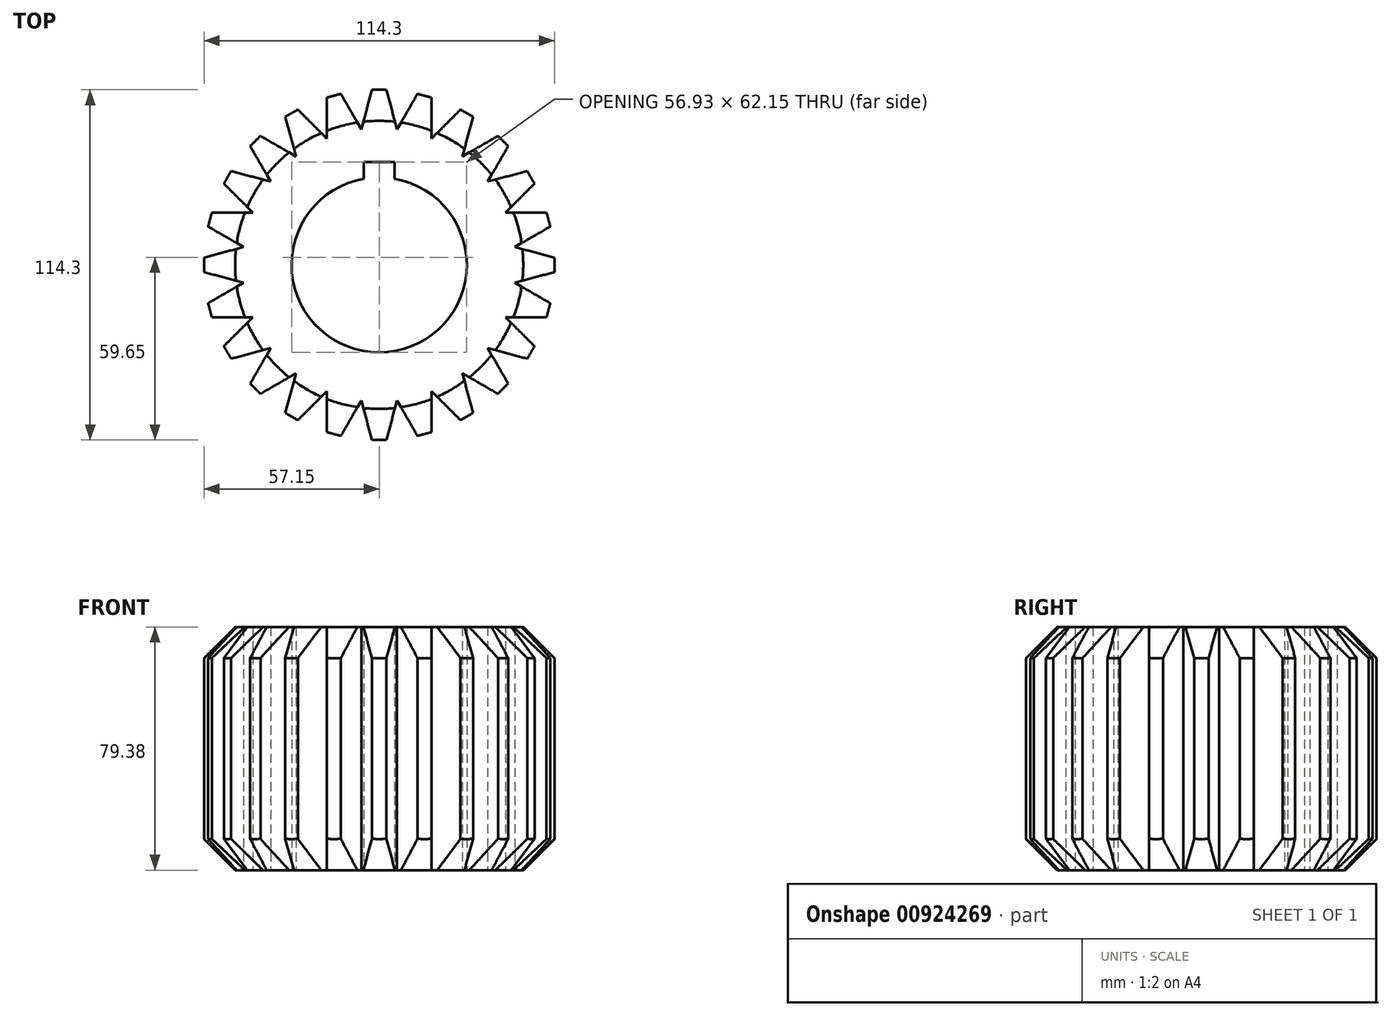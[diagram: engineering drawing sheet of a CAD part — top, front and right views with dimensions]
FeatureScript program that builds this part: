
annotation { "Feature Type Name" : "Feature", "Feature Type Description" : "" }
export const myFeature = defineFeature(function(context is Context, id is Id, definition is map)
    precondition{}
    {
        {
            var Q0;
            Q0=qCreatedBy(makeId("Top.planeOp"),FACE);
            var sketch = newSketch(context, id + "F0", { "sketchPlane" : qUnion([Q0])});
            skLineSegment(sketch, "E0", {"start": v(0, 57.15) * mm, "end": v(0, -57.15) * mm, "construction": true});
            skLineSegment(sketch, "E1", {"start": v(0, 0) * mm, "end": v(-7.32, 55.6) * mm, "construction": true});
            skLineSegment(sketch, "E2", {"start": v(-2.36, 57.15) * mm, "end": v(2.36, 57.15) * mm});
            skLineSegment(sketch, "E3", {"start": v(-2.36, 57.15) * mm, "end": v(-5.82, 44.23) * mm});
            skLineSegment(sketch, "E4.MirrorCS", {"start": v(-12.5, 55.81) * mm, "end": v(-5.82, 44.23) * mm});
            skLineSegment(sketch, "E5.MirrorCS", {"start": v(-12.5, 55.81) * mm, "end": v(-17.07, 54.6) * mm});
            skLineSegment(sketch, "E6.MirrorCS", {"start": v(-14.8, 55.2) * mm, "end": v(14.8, -55.2) * mm, "construction": true});
            skLineSegment(sketch, "E7.MirrorCS", {"start": v(2.36, 57.15) * mm, "end": v(5.82, 44.23) * mm});
            skLineSegment(sketch, "E8.MirrorCS", {"start": v(12.5, 55.81) * mm, "end": v(5.82, 44.23) * mm});
            skLineSegment(sketch, "E9.MirrorCS", {"start": v(12.5, 55.81) * mm, "end": v(17.07, 54.6) * mm});
            skLineSegment(sketch, "E10.MirrorCS", {"start": v(-17.07, 54.6) * mm, "end": v(-17.07, 41.22) * mm});
            skLineSegment(sketch, "E11.MirrorCS", {"start": v(17.07, 54.6) * mm, "end": v(17.07, 41.22) * mm});
            skLineSegment(sketch, "E12.MirrorCS", {"start": v(-28.58, 49.5) * mm, "end": v(28.58, -49.5) * mm, "construction": true});
            skLineSegment(sketch, "E13.MirrorCS", {"start": v(-38.74, 42.08) * mm, "end": v(-27.16, 35.4) * mm});
            skLineSegment(sketch, "E14.MirrorCS", {"start": v(-42.08, 38.74) * mm, "end": v(-35.4, 27.16) * mm});
            skLineSegment(sketch, "E15.MirrorCS", {"start": v(-42.08, 38.74) * mm, "end": v(-38.74, 42.08) * mm});
            skLineSegment(sketch, "E16.MirrorCS", {"start": v(-48.31, 30.62) * mm, "end": v(-35.4, 27.16) * mm});
            skLineSegment(sketch, "E17.MirrorCS", {"start": v(-48.31, 30.62) * mm, "end": v(-50.67, 26.53) * mm});
            skLineSegment(sketch, "E18.MirrorCS", {"start": v(-50.67, 26.53) * mm, "end": v(-41.22, 17.07) * mm});
            skLineSegment(sketch, "E19.MirrorCS", {"start": v(-54.6, 17.07) * mm, "end": v(-41.22, 17.07) * mm});
            skLineSegment(sketch, "E20.MirrorCS", {"start": v(-54.6, 17.07) * mm, "end": v(-55.81, 12.5) * mm});
            skLineSegment(sketch, "E21.MirrorCS", {"start": v(-55.81, 12.5) * mm, "end": v(-44.23, 5.82) * mm});
            skLineSegment(sketch, "E22.MirrorCS", {"start": v(-26.53, 50.67) * mm, "end": v(-17.07, 41.22) * mm});
            skLineSegment(sketch, "E23.MirrorCS", {"start": v(-30.62, 48.31) * mm, "end": v(-27.16, 35.4) * mm});
            skLineSegment(sketch, "E24.MirrorCS", {"start": v(-26.53, 50.67) * mm, "end": v(-30.62, 48.31) * mm});
            skLineSegment(sketch, "E25.MirrorCS", {"start": v(26.53, 50.67) * mm, "end": v(17.07, 41.22) * mm});
            skLineSegment(sketch, "E26.MirrorCS", {"start": v(26.53, 50.67) * mm, "end": v(30.62, 48.31) * mm});
            skLineSegment(sketch, "E27.MirrorCS", {"start": v(30.62, 48.31) * mm, "end": v(27.16, 35.4) * mm});
            skLineSegment(sketch, "E28.MirrorCS", {"start": v(38.74, 42.08) * mm, "end": v(27.16, 35.4) * mm});
            skLineSegment(sketch, "E29.MirrorCS", {"start": v(38.74, 42.08) * mm, "end": v(42.08, 38.74) * mm});
            skLineSegment(sketch, "E30.MirrorCS", {"start": v(42.08, 38.74) * mm, "end": v(35.4, 27.16) * mm});
            skLineSegment(sketch, "E31.MirrorCS", {"start": v(-57.15, 2.36) * mm, "end": v(-44.23, 5.82) * mm});
            skLineSegment(sketch, "E32.MirrorCS", {"start": v(-57.15, -2.36) * mm, "end": v(-44.23, -5.82) * mm});
            skLineSegment(sketch, "E33.MirrorCS", {"start": v(-57.15, 2.36) * mm, "end": v(-57.15, -2.36) * mm});
            skLineSegment(sketch, "E34", {"start": v(57.15, 0) * mm, "end": v(-57.15, 0) * mm, "construction": true});
            skLineSegment(sketch, "E35.MirrorCS", {"start": v(-55.81, -12.5) * mm, "end": v(-44.23, -5.82) * mm});
            skLineSegment(sketch, "E36.MirrorCS", {"start": v(-54.6, -17.07) * mm, "end": v(-55.81, -12.5) * mm});
            skLineSegment(sketch, "E37.MirrorCS", {"start": v(-50.67, -26.53) * mm, "end": v(-41.22, -17.07) * mm});
            skLineSegment(sketch, "E38.MirrorCS", {"start": v(-48.31, -30.62) * mm, "end": v(-50.67, -26.53) * mm});
            skLineSegment(sketch, "E39.MirrorCS", {"start": v(-48.31, -30.62) * mm, "end": v(-35.4, -27.16) * mm});
            skLineSegment(sketch, "E40.MirrorCS", {"start": v(-42.08, -38.74) * mm, "end": v(-35.4, -27.16) * mm});
            skLineSegment(sketch, "E41.MirrorCS", {"start": v(-42.08, -38.74) * mm, "end": v(-38.74, -42.08) * mm});
            skLineSegment(sketch, "E42.MirrorCS", {"start": v(-38.74, -42.08) * mm, "end": v(-27.16, -35.4) * mm});
            skLineSegment(sketch, "E43.MirrorCS", {"start": v(-30.62, -48.31) * mm, "end": v(-27.16, -35.4) * mm});
            skLineSegment(sketch, "E44.MirrorCS", {"start": v(-26.53, -50.67) * mm, "end": v(-30.62, -48.31) * mm});
            skLineSegment(sketch, "E45.MirrorCS", {"start": v(-26.53, -50.67) * mm, "end": v(-17.07, -41.22) * mm});
            skLineSegment(sketch, "E46.MirrorCS", {"start": v(-17.07, -54.6) * mm, "end": v(-17.07, -41.22) * mm});
            skLineSegment(sketch, "E47.MirrorCS", {"start": v(-14.8, -55.2) * mm, "end": v(14.8, 55.2) * mm, "construction": true});
            skLineSegment(sketch, "E48.MirrorCS", {"start": v(-12.5, -55.81) * mm, "end": v(-17.07, -54.6) * mm});
            skLineSegment(sketch, "E49.MirrorCS", {"start": v(-12.5, -55.81) * mm, "end": v(-5.82, -44.23) * mm});
            skLineSegment(sketch, "E50.MirrorCS", {"start": v(-2.36, -57.15) * mm, "end": v(-5.82, -44.23) * mm});
            skLineSegment(sketch, "E51.MirrorCS", {"start": v(-2.36, -57.15) * mm, "end": v(2.36, -57.15) * mm});
            skLineSegment(sketch, "E52.MirrorCS", {"start": v(-54.6, -17.07) * mm, "end": v(-41.22, -17.07) * mm});
            skLineSegment(sketch, "E53.MirrorCS", {"start": v(2.36, -57.15) * mm, "end": v(5.82, -44.23) * mm});
            skLineSegment(sketch, "E54.MirrorCS", {"start": v(12.5, -55.81) * mm, "end": v(17.07, -54.6) * mm});
            skLineSegment(sketch, "E55.MirrorCS", {"start": v(17.07, -54.6) * mm, "end": v(17.07, -41.22) * mm});
            skLineSegment(sketch, "E56.MirrorCS", {"start": v(26.53, -50.67) * mm, "end": v(17.07, -41.22) * mm});
            skLineSegment(sketch, "E57.MirrorCS", {"start": v(26.53, -50.67) * mm, "end": v(30.62, -48.31) * mm});
            skLineSegment(sketch, "E58.MirrorCS", {"start": v(30.62, -48.31) * mm, "end": v(27.16, -35.4) * mm});
            skLineSegment(sketch, "E59.MirrorCS", {"start": v(12.5, -55.81) * mm, "end": v(5.82, -44.23) * mm});
            skLineSegment(sketch, "E60.MirrorCS", {"start": v(38.74, -42.08) * mm, "end": v(27.16, -35.4) * mm});
            skLineSegment(sketch, "E61.MirrorCS", {"start": v(42.08, -38.74) * mm, "end": v(38.74, -42.08) * mm});
            skLineSegment(sketch, "E62.MirrorCS", {"start": v(42.08, -38.74) * mm, "end": v(35.4, -27.16) * mm});
            skLineSegment(sketch, "E63.MirrorCS", {"start": v(48.31, -30.62) * mm, "end": v(35.4, -27.16) * mm});
            skLineSegment(sketch, "E64.MirrorCS", {"start": v(48.31, -30.62) * mm, "end": v(50.67, -26.53) * mm});
            skLineSegment(sketch, "E65.MirrorCS", {"start": v(50.67, -26.53) * mm, "end": v(41.22, -17.07) * mm});
            skLineSegment(sketch, "E66.MirrorCS", {"start": v(54.6, -17.07) * mm, "end": v(41.22, -17.07) * mm});
            skLineSegment(sketch, "E67.MirrorCS", {"start": v(54.6, -17.07) * mm, "end": v(55.81, -12.5) * mm});
            skLineSegment(sketch, "E68.MirrorCS", {"start": v(55.81, -12.5) * mm, "end": v(44.23, -5.82) * mm});
            skLineSegment(sketch, "E69.MirrorCS", {"start": v(57.15, -2.36) * mm, "end": v(44.23, -5.82) * mm});
            skLineSegment(sketch, "E70.MirrorCS", {"start": v(57.15, 2.36) * mm, "end": v(57.15, -2.36) * mm});
            skLineSegment(sketch, "E71.MirrorCS", {"start": v(57.15, 2.36) * mm, "end": v(44.23, 5.82) * mm});
            skLineSegment(sketch, "E72.MirrorCS", {"start": v(55.81, 12.5) * mm, "end": v(44.23, 5.82) * mm});
            skLineSegment(sketch, "E73.MirrorCS", {"start": v(54.6, 17.07) * mm, "end": v(55.81, 12.5) * mm});
            skLineSegment(sketch, "E74.MirrorCS", {"start": v(48.31, 30.62) * mm, "end": v(35.4, 27.16) * mm});
            skLineSegment(sketch, "E75.MirrorCS", {"start": v(54.6, 17.07) * mm, "end": v(41.22, 17.07) * mm});
            skLineSegment(sketch, "E76.MirrorCS", {"start": v(50.67, 26.53) * mm, "end": v(41.22, 17.07) * mm});
            skLineSegment(sketch, "E77.MirrorCS", {"start": v(48.31, 30.62) * mm, "end": v(50.67, 26.53) * mm});
            skLineSegment(sketch, "E78", {"start": v(0, 28.57) * mm, "end": v(0, 33.58) * mm, "construction": true});
            skLineSegment(sketch, "E79", {"start": v(5, 33.58) * mm, "end": v(-5, 33.58) * mm});
            skLineSegment(sketch, "E80", {"start": v(5, 33.58) * mm, "end": v(5, 28.13) * mm});
            skLineSegment(sketch, "E81.MirrorCS", {"start": v(-5, 33.58) * mm, "end": v(-5, 28.13) * mm});
            skArc(sketch, "E82", {"start": v(5, 28.13) * mm, "mid": v(0, 28.57) * mm, "end": v(-5, 28.13) * mm, "construction": true});
            skArc(sketch, "E83", {"start": v(-5, 28.13) * mm, "mid": v(0, -28.58) * mm, "end": v(5, 28.13) * mm});
            skSolve(sketch);
        }
        {
            var Q0;
            Q0=makeQuery(id+"F0.imprint","IMPRINT",FACE,{"disambiguationData":[TD([[makeQuery(id+"F0.imprint","IMPRINT",EDGE,{"derivedFrom":sQuery(id+"F0.wireOp",EDGE,"E2")}),-1.0]])]});
            extrude(context, id + "F1", {"entities" : qUnion([Q0]), "depth" : 79.38 * mm, "offsetDistance" : 25 * mm});
        }
        {
            var Q0;
            Q0=qCreatedBy(makeId("Front.planeOp"),FACE);
            var sketch = newSketch(context, id + "F2", { "sketchPlane" : qUnion([Q0])});
            skLineSegment(sketch, "E84", {"start": v(-47, 0) * mm, "end": v(47, 0) * mm, "construction": true});
            skLineSegment(sketch, "E85", {"start": v(0, 0) * mm, "end": v(0, 79.38) * mm, "construction": true});
            skLineSegment(sketch, "E86", {"start": v(-47, 39.69) * mm, "end": v(47, 39.69) * mm, "construction": true});
            skPoint(sketch, "E86.startSnap0", {"position": v(0, 39.69) * mm});
            skLineSegment(sketch, "E87", {"start": v(-47, 79.38) * mm, "end": v(47, 79.38) * mm, "construction": true});
            skLineSegment(sketch, "E88", {"start": v(0, 126.37) * mm, "end": v(-86.68, 39.69) * mm});
            skLineSegment(sketch, "E89", {"start": v(-86.68, 39.69) * mm, "end": v(0, -47) * mm});
            skLineSegment(sketch, "E90", {"start": v(0, 126.37) * mm, "end": v(0, -46.99) * mm});
            skSolve(sketch);
        }
        {
            var Q0;
            Q0=makeQuery(id+"F2.imprint","IMPRINT",FACE,{"disambiguationData":[TD([[makeQuery(id+"F2.imprint","IMPRINT",EDGE,{"derivedFrom":sQuery(id+"F2.wireOp",EDGE,"E88")}),1.0]])]});
            var Q1;
            Q1=sQuery(id+"F2.wireOp",EDGE,"E88");
            var Q2;
            Q2=sQuery(id+"F2.wireOp",EDGE,"E89");
            var Q3;
            Q3=sQuery(id+"F2.wireOp",EDGE,"E90");
            revolve(context, id + "F3", {"operationType" : NewBodyOperationType.INTERSECT, "surfaceOperationType" : NewSurfaceOperationType.NEW, "entities" : qUnion([Q0]), "surfaceEntities" : qUnion([Q1, Q2]), "axis" : qUnion([Q3]), "revolveType" : RevolveType.FULL});
        }
    });
